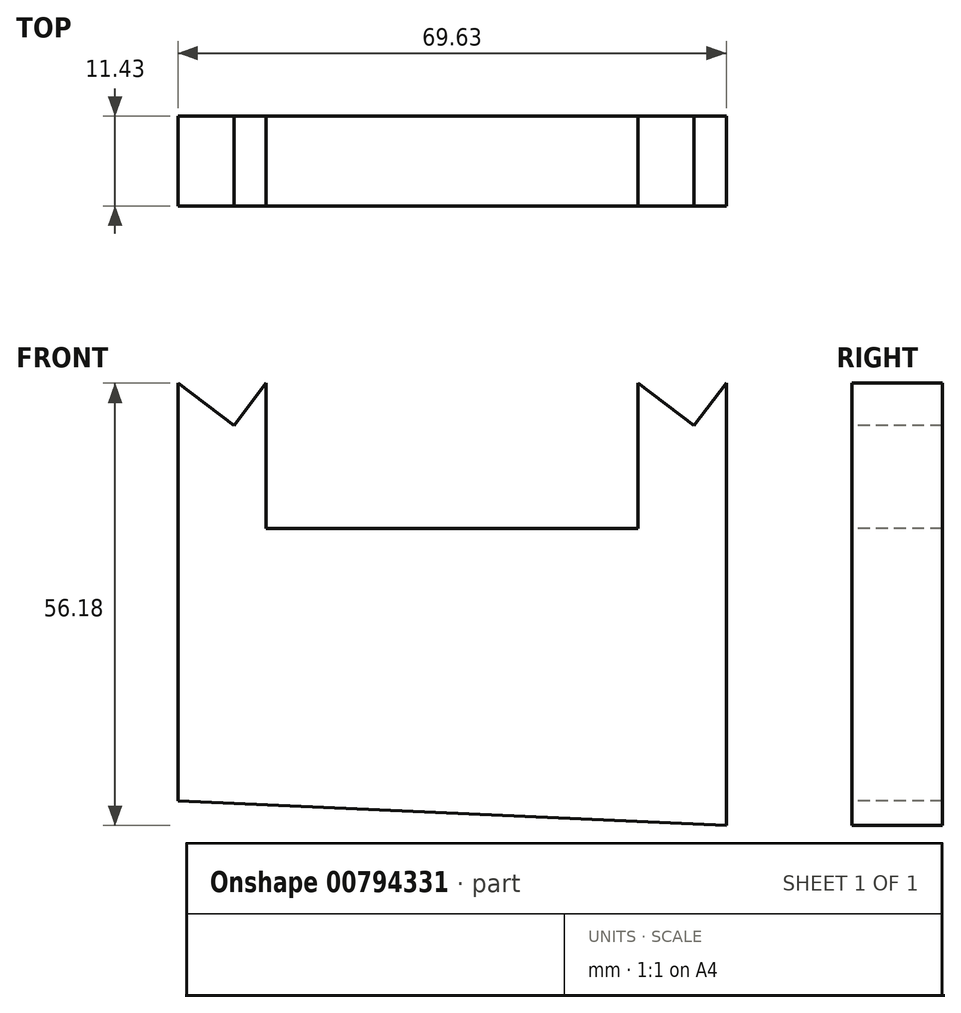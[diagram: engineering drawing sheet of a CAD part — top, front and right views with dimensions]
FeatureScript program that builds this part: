
annotation { "Feature Type Name" : "Feature", "Feature Type Description" : "" }
export const myFeature = defineFeature(function(context is Context, id is Id, definition is map)
    precondition{}
    {
        {
            var Q0;
            Q0=qCreatedBy(makeId("Front.planeOp"),FACE);
            var sketch = newSketch(context, id + "F0", { "sketchPlane" : qUnion([Q0])});
            skLineSegment(sketch, "E0", {"start": v(-42.13, 25.1) * mm, "end": v(-42.13, -27.95) * mm});
            skLineSegment(sketch, "E1", {"start": v(-42.13, 25.1) * mm, "end": v(-35.04, 19.72) * mm});
            skLineSegment(sketch, "E2", {"start": v(-35.04, 19.72) * mm, "end": v(-30.94, 25.1) * mm});
            skLineSegment(sketch, "E3", {"start": v(-30.94, 25.1) * mm, "end": v(-30.94, 6.67) * mm});
            skLineSegment(sketch, "E4", {"start": v(-30.94, 6.67) * mm, "end": v(16.31, 6.67) * mm});
            skLineSegment(sketch, "E5", {"start": v(16.31, 6.67) * mm, "end": v(16.31, 25.1) * mm});
            skLineSegment(sketch, "E6", {"start": v(16.31, 25.1) * mm, "end": v(23.4, 19.72) * mm});
            skLineSegment(sketch, "E7", {"start": v(23.4, 19.72) * mm, "end": v(27.5, 25.1) * mm});
            skLineSegment(sketch, "E8", {"start": v(27.5, 25.1) * mm, "end": v(27.5, 6.67) * mm});
            skLineSegment(sketch, "E9", {"start": v(27.5, 6.67) * mm, "end": v(27.5, -31.07) * mm});
            skLineSegment(sketch, "E10", {"start": v(27.5, -31.07) * mm, "end": v(-42.13, -27.95) * mm});
            skSolve(sketch);
        }
        {
            var Q0;
            Q0=makeQuery(id+"F0.imprint","IMPRINT",FACE,{"disambiguationData":[TD([[makeQuery(id+"F0.imprint","IMPRINT",EDGE,{"derivedFrom":sQuery(id+"F0.wireOp",EDGE,"E0")}),1.0]])]});
            extrude(context, id + "F1", {"entities" : qUnion([Q0]), "oppositeDirection" : true, "depth" : 11.43 * mm, "offsetDistance" : 25.4 * mm});
        }
    });
